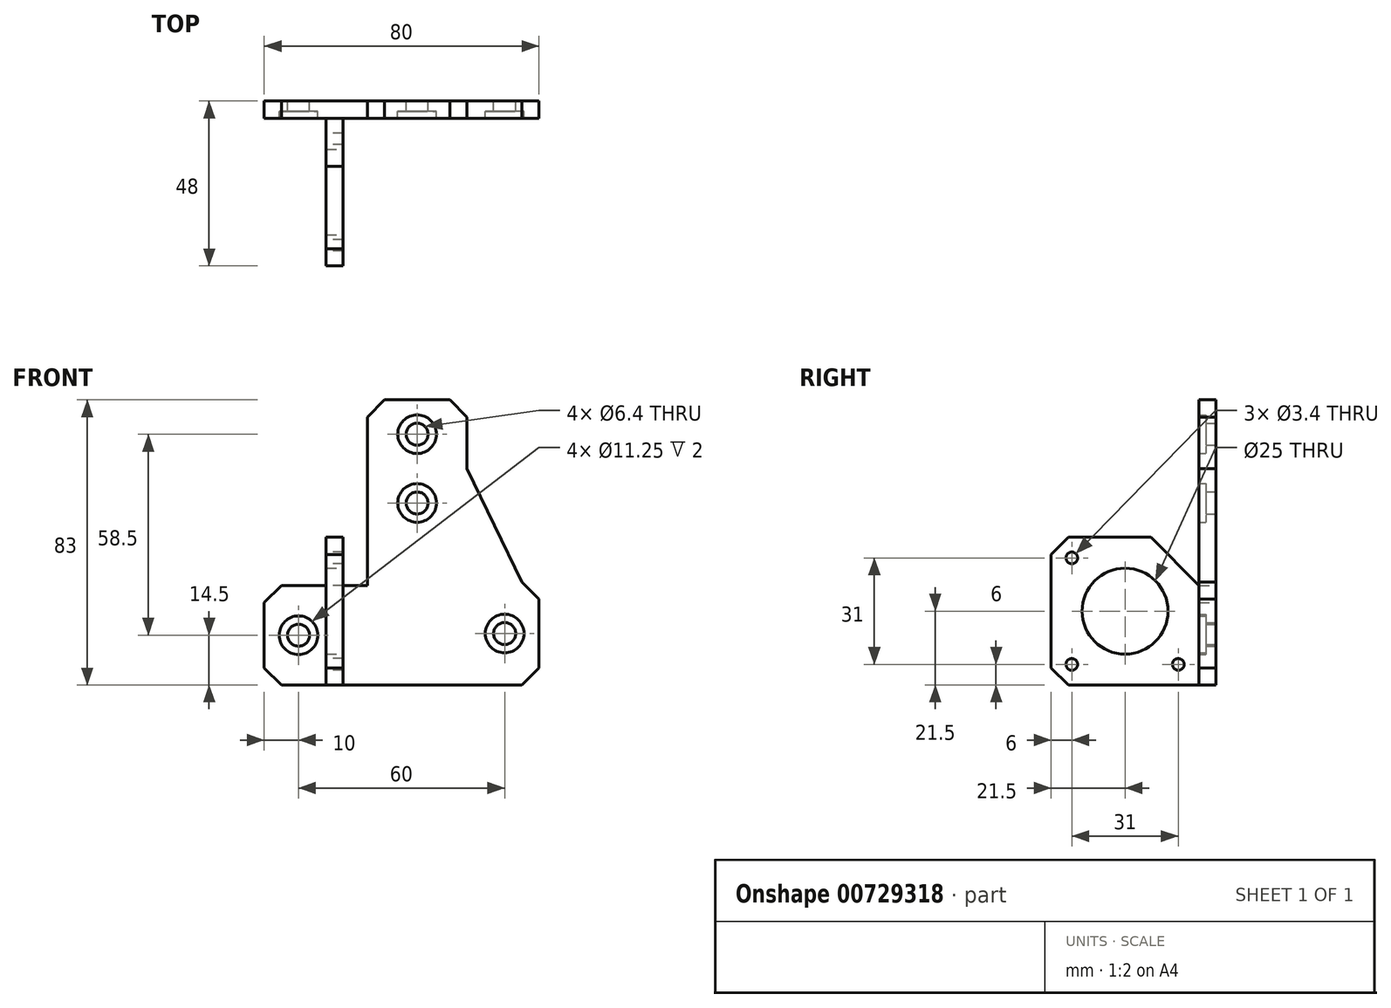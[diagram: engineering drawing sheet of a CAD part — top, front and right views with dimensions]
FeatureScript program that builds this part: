
annotation { "Feature Type Name" : "Feature", "Feature Type Description" : "" }
export const myFeature = defineFeature(function(context is Context, id is Id, definition is map)
    precondition{}
    {
        {
            var Q0;
            Q0=qCreatedBy(makeId("Front.planeOp"),FACE);
            var sketch = newSketch(context, id + "F0", { "sketchPlane" : qUnion([Q0])});
            skLineSegment(sketch, "E0", {"start": v(0, 0) * mm, "end": v(80, 0) * mm});
            skLineSegment(sketch, "E1", {"start": v(80, 0) * mm, "end": v(80, 30) * mm});
            skLineSegment(sketch, "E2", {"start": v(80, 30) * mm, "end": v(75, 30) * mm});
            skLineSegment(sketch, "E3", {"start": v(59, 63) * mm, "end": v(75, 30) * mm});
            skLineSegment(sketch, "E4", {"start": v(59, 63) * mm, "end": v(59, 83) * mm});
            skLineSegment(sketch, "E5", {"start": v(59, 83) * mm, "end": v(30, 83) * mm});
            skLineSegment(sketch, "E6", {"start": v(30, 83) * mm, "end": v(30, 43) * mm});
            skLineSegment(sketch, "E7", {"start": v(30, 43) * mm, "end": v(18, 43) * mm});
            skLineSegment(sketch, "E8", {"start": v(0, 29) * mm, "end": v(0, 0) * mm});
            skLineSegment(sketch, "E9", {"start": v(0, 29) * mm, "end": v(18, 29) * mm});
            skLineSegment(sketch, "E10", {"start": v(18, 29) * mm, "end": v(18, 43) * mm});
            skPoint(sketch, "E11.centerSnap0", {"position": v(44.5, 83) * mm});
            skPoint(sketch, "E12.centerSnap0", {"position": v(0, 14.5) * mm});
            skPoint(sketch, "E13.centerSnap0", {"position": v(80, 15) * mm});
            skPoint(sketch, "E14", {"position": v(44.5, 73) * mm});
            skPoint(sketch, "E15", {"position": v(44.5, 53) * mm});
            skPoint(sketch, "E16", {"position": v(10, 14.5) * mm});
            skPoint(sketch, "E17", {"position": v(70, 15) * mm});
            skSolve(sketch);
        }
        {
            var Q0;
            Q0=makeQuery(id+"F0.imprint","IMPRINT",FACE,{"disambiguationData":[TD([[makeQuery(id+"F0.imprint","IMPRINT",EDGE,{"derivedFrom":sQuery(id+"F0.wireOp",EDGE,"E0")}),1.0]])]});
            extrude(context, id + "F1", {"entities" : qUnion([Q0]), "oppositeDirection" : true, "depth" : 5 * mm, "offsetDistance" : 25 * mm});
        }
        {
            var Q0;
            Q0=sQuery(id+"F0.wireOp",VERTEX,"E16");
            var Q1;
            Q1=sQuery(id+"F0.wireOp",VERTEX,"E15");
            var Q2;
            Q2=sQuery(id+"F0.wireOp",VERTEX,"E14");
            var Q3;
            Q3=sQuery(id+"F0.wireOp",VERTEX,"E17");
            var Q4;
            Q4=makeQuery(id+"F1.opExtrude","SWEPT_BODY",BODY,{"disambiguationData":[OSD([sQuery(id+"F0.wireOp",EDGE,"E0"),sQuery(id+"F0.wireOp",EDGE,"E1"),sQuery(id+"F0.wireOp",EDGE,"E2"),sQuery(id+"F0.wireOp",EDGE,"E3"),sQuery(id+"F0.wireOp",EDGE,"E4"),sQuery(id+"F0.wireOp",EDGE,"E5"),sQuery(id+"F0.wireOp",EDGE,"E6"),sQuery(id+"F0.wireOp",EDGE,"E7"),sQuery(id+"F0.wireOp",EDGE,"E8"),sQuery(id+"F0.wireOp",EDGE,"E9"),sQuery(id+"F0.wireOp",EDGE,"E10")])]});
            hole(context, id + "F2", {"style" : HoleStyle.C_BORE, "endStyle" : HoleEndStyle.THROUGH, "holeDiameter" : 6.4 * mm, "cBoreDiameter" : 11.25 * mm, "cBoreDepth" : 2 * mm, "majorDiameter" : 5 * mm, "isTappedThrough" : true, "tappedDepth" : 12 * mm, "tapClearance" : 3, "locations" : qUnion([Q0, Q1, Q2, Q3]), "scope" : qUnion([Q4])});
        }
        {
            var Q0;
            Q0=makeQuery(id+"F0.imprint","IMPRINT",FACE,{"disambiguationData":[TD([[makeQuery(id+"F0.imprint","IMPRINT",EDGE,{"derivedFrom":sQuery(id+"F0.wireOp",EDGE,"E0")}),1.0]])]});
            var sketch = newSketch(context, id + "F3", { "sketchPlane" : qUnion([Q0])});
            skLineSegment(sketch, "E18.bottom", {"start": v(18, 43) * mm, "end": v(23, 43) * mm});
            skLineSegment(sketch, "E18.top", {"start": v(18, 0) * mm, "end": v(23, 0) * mm});
            skLineSegment(sketch, "E18.left", {"start": v(18, 43) * mm, "end": v(18, 0) * mm});
            skLineSegment(sketch, "E18.right", {"start": v(23, 43) * mm, "end": v(23, 0) * mm});
            skSolve(sketch);
        }
        {
            var Q0;
            Q0 = qSketchRegion(id + "F3", true);
            extrude(context, id + "F4", {"entities" : qUnion([Q0]), "operationType" : NewBodyOperationType.ADD, "depth" : 43 * mm, "offsetDistance" : 25 * mm});
        }
        {
            var Q0;
            Q0=makeQuery(id+"F4.opExtrude","SWEPT_FACE",FACE,{"disambiguationData":[OSD([sQuery(id+"F3.wireOp",EDGE,"E18.right")])]});
            var sketch = newSketch(context, id + "F5", { "sketchPlane" : qUnion([Q0])});
            skLineSegment(sketch, "E19", {"start": v(0, 43) * mm, "end": v(-43, 0) * mm, "construction": true});
            skPoint(sketch, "E20", {"position": v(-21.5, 21.5) * mm});
            skLineSegment(sketch, "E21.bottom", {"start": v(-37, 37) * mm, "end": v(-6, 37) * mm, "construction": true});
            skLineSegment(sketch, "E21.top", {"start": v(-37, 6) * mm, "end": v(-6, 6) * mm, "construction": true});
            skLineSegment(sketch, "E21.left", {"start": v(-37, 37) * mm, "end": v(-37, 6) * mm, "construction": true});
            skLineSegment(sketch, "E21.right", {"start": v(-6, 37) * mm, "end": v(-6, 6) * mm, "construction": true});
            skPoint(sketch, "E22", {"position": v(-6, 37) * mm});
            skPoint(sketch, "E23", {"position": v(-6, 6) * mm});
            skPoint(sketch, "E24", {"position": v(-37, 6) * mm});
            skCircle(sketch, "E25", {"center": v(-21.5, 21.5) * mm, "radius": 12.5 * mm});
            skSolve(sketch);
        }
        {
            var Q0;
            Q0=sQuery(id+"F5.wireOp",VERTEX,"E21.bottom.start");
            var Q1;
            Q1=sQuery(id+"F5.wireOp",VERTEX,"E23");
            var Q2;
            Q2=sQuery(id+"F5.wireOp",VERTEX,"E24");
            var Q3;
            Q3=makeQuery(id+"F1.opExtrude","SWEPT_BODY",BODY,{"disambiguationData":[OSD([sQuery(id+"F0.wireOp",EDGE,"E0"),sQuery(id+"F0.wireOp",EDGE,"E1"),sQuery(id+"F0.wireOp",EDGE,"E2"),sQuery(id+"F0.wireOp",EDGE,"E3"),sQuery(id+"F0.wireOp",EDGE,"E4"),sQuery(id+"F0.wireOp",EDGE,"E5"),sQuery(id+"F0.wireOp",EDGE,"E6"),sQuery(id+"F0.wireOp",EDGE,"E7"),sQuery(id+"F0.wireOp",EDGE,"E8"),sQuery(id+"F0.wireOp",EDGE,"E9"),sQuery(id+"F0.wireOp",EDGE,"E10")])]});
            hole(context, id + "F6", {"style" : HoleStyle.SIMPLE, "endStyle" : HoleEndStyle.THROUGH, "standardTappedOrClearance" : lookupTablePath({ "fit" : "Normal", "standard" : "ISO", "size" : "M3", "type" : "Clearance" }), "standardBlindInLast" : lookupTablePath({ "fit" : "Normal", "standard" : "ISO", "engagement" : "75%", "pitch" : "0.5 mm", "size" : "M3", "type" : "Clearance & tapped" }), "holeDiameter" : 3.4 * mm, "majorDiameter" : 5 * mm, "isTappedThrough" : true, "tappedDepth" : 12 * mm, "tapClearance" : 3, "locations" : qUnion([Q0, Q1, Q2]), "scope" : qUnion([Q3])});
        }
        {
            var Q0;
            Q0=makeQuery(id+"F5.imprint","IMPRINT",FACE,{"disambiguationData":[TD([[makeQuery(id+"F5.imprint","IMPRINT",EDGE,{"derivedFrom":sQuery(id+"F5.wireOp",EDGE,"E25")}),1.0]])]});
            extrude(context, id + "F7", {"entities" : qUnion([Q0]), "operationType" : NewBodyOperationType.REMOVE, "endBound" : BoundingType.THROUGH_ALL, "oppositeDirection" : true, "depth" : 25 * mm, "offsetDistance" : 25 * mm});
        }
        {
            var Q0;
            Q0=makeQuery(id+"F1.opExtrude","CAP_FACE",FACE,{"disambiguationData":[OSD([sQuery(id+"F0.wireOp",EDGE,"E0"),sQuery(id+"F0.wireOp",EDGE,"E1"),sQuery(id+"F0.wireOp",EDGE,"E2"),sQuery(id+"F0.wireOp",EDGE,"E3"),sQuery(id+"F0.wireOp",EDGE,"E4"),sQuery(id+"F0.wireOp",EDGE,"E5"),sQuery(id+"F0.wireOp",EDGE,"E6"),sQuery(id+"F0.wireOp",EDGE,"E7"),sQuery(id+"F0.wireOp",EDGE,"E8"),sQuery(id+"F0.wireOp",EDGE,"E9"),sQuery(id+"F0.wireOp",EDGE,"E10")])],"isStart":false});
            var sketch = newSketch(context, id + "F8", { "sketchPlane" : qUnion([Q0])});
            skPoint(sketch, "E26", {"position": v(-44.5, 15) * mm});
            skSolve(sketch);
        }
        {
            var Q0;
            Q0=makeQuery(id+"F4.boolean.opBoolean","MERGE",FACE,{"derivedFrom":[makeQuery(id+"F1.opExtrude","SWEPT_FACE",FACE,{"disambiguationData":[OSD([sQuery(id+"F0.wireOp",EDGE,"E10")])]}),makeQuery(id+"F4.opExtrude","SWEPT_FACE",FACE,{"disambiguationData":[OSD([sQuery(id+"F3.wireOp",EDGE,"E18.left")])]})]});
            var sketch = newSketch(context, id + "F9", { "sketchPlane" : qUnion([Q0])});
            skLineSegment(sketch, "E27", {"start": v(-5, 43) * mm, "end": v(-5, 29) * mm});
            skLineSegment(sketch, "E28", {"start": v(-5, 29) * mm, "end": v(0, 29) * mm});
            skLineSegment(sketch, "E29", {"start": v(0, 29) * mm, "end": v(14, 43) * mm});
            skLineSegment(sketch, "E30", {"start": v(14, 43) * mm, "end": v(-5, 43) * mm});
            skSolve(sketch);
        }
        {
            var Q0;
            Q0=makeQuery(id+"F9.imprint","IMPRINT",FACE,{"disambiguationData":[TD([[makeQuery(id+"F9.imprint","IMPRINT",EDGE,{"derivedFrom":sQuery(id+"F9.wireOp",EDGE,"NspiHNFW-mcFe-9KOU-FHq9-gv2RlaPcV06F")}),-1.0]])]});
            var Q1;
            Q1=makeQuery(id+"F9.imprint","IMPRINT",FACE,{"disambiguationData":[TD([[makeQuery(id+"F9.imprint","IMPRINT",EDGE,{"derivedFrom":sQuery(id+"F9.wireOp",EDGE,"E27")}),-1.0]])]});
            var Q2;
            Q2=makeQuery(id+"F1.opExtrude","SWEPT_FACE",FACE,{"disambiguationData":[OSD([sQuery(id+"F0.wireOp",EDGE,"E6")])]});
            extrude(context, id + "F10", {"entities" : qUnion([Q0, Q1]), "operationType" : NewBodyOperationType.REMOVE, "endBound" : BoundingType.UP_TO_SURFACE, "oppositeDirection" : true, "depth" : 25 * mm, "endBoundEntityFace" : qUnion([Q2]), "offsetDistance" : 25 * mm});
        }
        {
            var Q0;
            Q0=makeQuery(id+"F1.opExtrude","SWEPT_EDGE",EDGE,{"disambiguationData":[OSD([sQuery(id+"F0.wireOp",EDGE,"E5"),sQuery(id+"F0.wireOp",EDGE,"E6")])]});
            var Q1;
            Q1=makeQuery(id+"F1.opExtrude","SWEPT_EDGE",EDGE,{"disambiguationData":[OSD([sQuery(id+"F0.wireOp",EDGE,"E4"),sQuery(id+"F0.wireOp",EDGE,"E5")])]});
            var Q2;
            Q2=makeQuery(id+"F1.opExtrude","SWEPT_EDGE",EDGE,{"disambiguationData":[OSD([sQuery(id+"F0.wireOp",EDGE,"E1"),sQuery(id+"F0.wireOp",EDGE,"E2")])]});
            var Q3;
            Q3=makeQuery(id+"F1.opExtrude","SWEPT_EDGE",EDGE,{"disambiguationData":[OSD([sQuery(id+"F0.wireOp",EDGE,"E0"),sQuery(id+"F0.wireOp",EDGE,"E1")])]});
            var Q4;
            Q4=makeQuery(id+"F4.opExtrude","CAP_EDGE",EDGE,{"disambiguationData":[OSD([sQuery(id+"F3.wireOp",EDGE,"E18.top")])],"isStart":false});
            var Q5;
            Q5=makeQuery(id+"F1.opExtrude","SWEPT_EDGE",EDGE,{"disambiguationData":[OSD([sQuery(id+"F0.wireOp",EDGE,"E0"),sQuery(id+"F0.wireOp",EDGE,"E8")])]});
            var Q6;
            Q6=makeQuery(id+"F1.opExtrude","SWEPT_EDGE",EDGE,{"disambiguationData":[OSD([sQuery(id+"F0.wireOp",EDGE,"E8"),sQuery(id+"F0.wireOp",EDGE,"E9")])]});
            var Q7;
            Q7=makeQuery(id+"F4.opExtrude","CAP_EDGE",EDGE,{"disambiguationData":[OSD([sQuery(id+"F3.wireOp",EDGE,"E18.bottom")])],"isStart":false});
            chamfer(context, id + "F11", {"entities" : qUnion([Q0, Q1, Q2, Q3, Q4, Q5, Q6, Q7]), "width" : 5 * mm, "tangentPropagation" : true});
        }
    });
